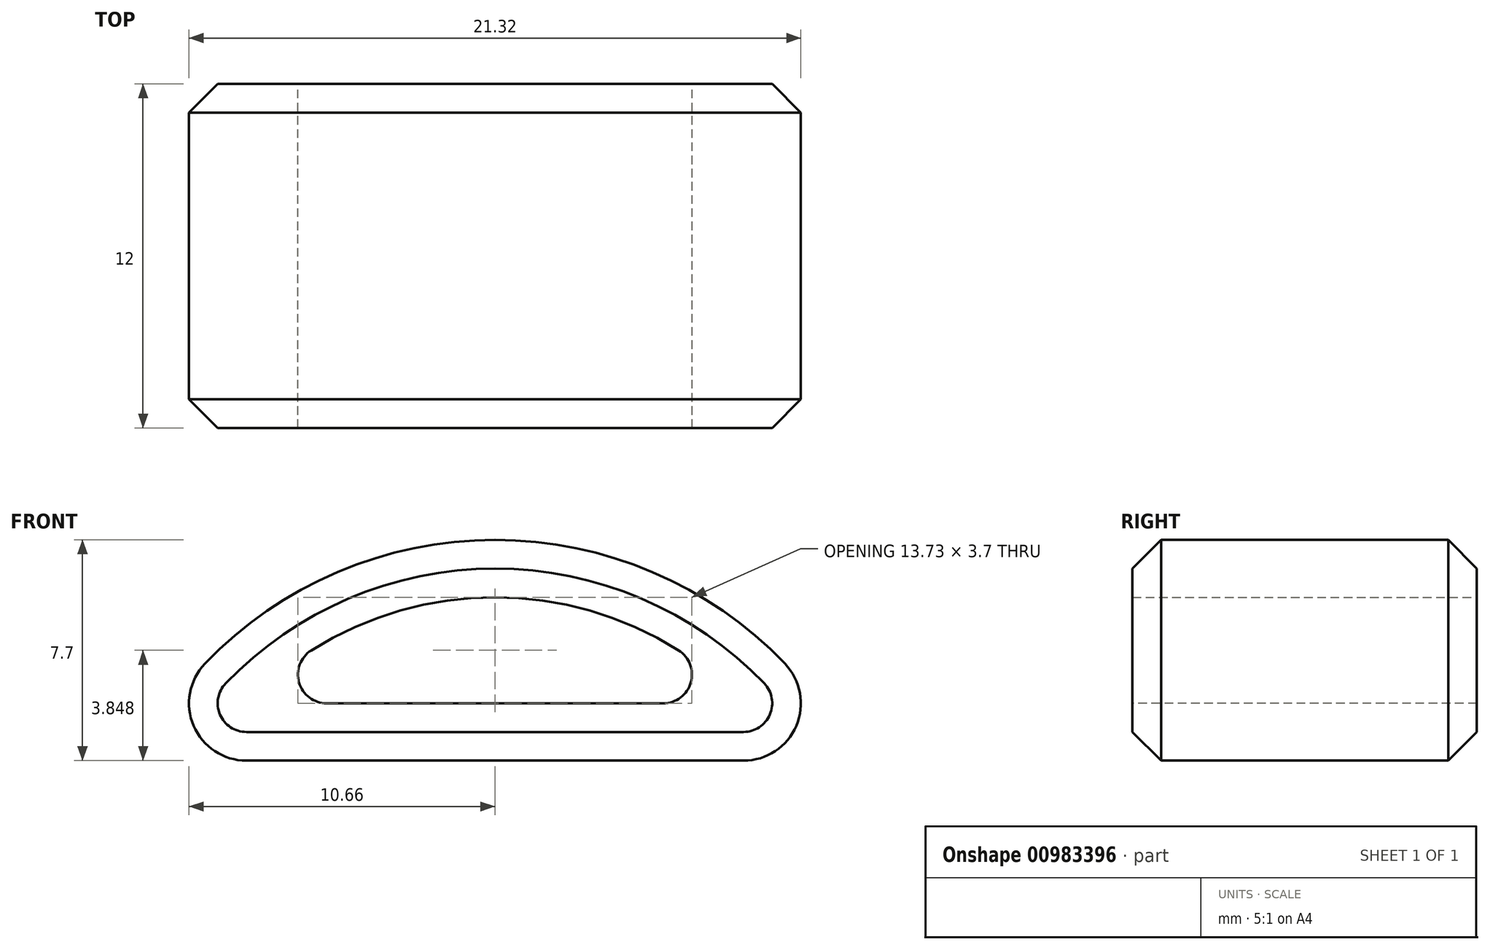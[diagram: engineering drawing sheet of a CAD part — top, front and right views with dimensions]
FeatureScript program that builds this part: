
annotation { "Feature Type Name" : "Feature", "Feature Type Description" : "" }
export const myFeature = defineFeature(function(context is Context, id is Id, definition is map)
    precondition{}
    {
        {
            var Q0;
            Q0=qCreatedBy(makeId("Front.planeOp"),FACE);
            var sketch = newSketch(context, id + "F0", { "sketchPlane" : qUnion([Q0])});
            skArc(sketch, "E0", {"start": v(12.5, 0) * mm, "mid": v(0, 7.7) * mm, "end": v(-12.5, 0) * mm});
            skLineSegment(sketch, "E1", {"start": v(-12.5, 0) * mm, "end": v(12.5, 0) * mm});
            skSolve(sketch);
        }
        {
            var Q0;
            Q0=makeQuery(id+"F0.imprint","IMPRINT",FACE,{"disambiguationData":[TD([[makeQuery(id+"F0.imprint","IMPRINT",EDGE,{"derivedFrom":sQuery(id+"F0.wireOp",EDGE,"E0")}),1.0]])]});
            extrude(context, id + "F1", {"entities" : qUnion([Q0]), "depth" : 12 * mm, "offsetDistance" : 25 * mm});
        }
        {
            var Q0;
            Q0=makeQuery(id+"F1.opExtrude","CAP_FACE",FACE,{"disambiguationData":[OSD([sQuery(id+"F0.wireOp",EDGE,"E0"),sQuery(id+"F0.wireOp",EDGE,"E1")])],"isStart":false});
            var Q1;
            Q1=makeQuery(id+"F1.opExtrude","CAP_FACE",FACE,{"disambiguationData":[OSD([sQuery(id+"F0.wireOp",EDGE,"E0"),sQuery(id+"F0.wireOp",EDGE,"E1")])],"isStart":true});
            shell(context, id + "F2", {"entities" : qUnion([Q0, Q1]), "thickness" : 2 * mm});
        }
        {
            var Q0;
            {var subQ0=sQuery(id+"F0.wireOp",EDGE,"E1");var subQ1=sQuery(id+"F0.wireOp",EDGE,"E0");Q0=makeQuery(id+"F1.opExtrude","SWEPT_EDGE",EDGE,{"disambiguationData":[OSD([subQ1,subQ0]),TDD([makeQuery(id+"F0.imprint","INTERSECT",VERTEX,{"disambiguationData":[OD(1.0)],"derivedFrom":[subQ1,subQ0]})])]});}
            var Q1;
            {var subQ0=sQuery(id+"F0.wireOp",EDGE,"E1");var subQ1=sQuery(id+"F0.wireOp",EDGE,"E0");Q1=makeQuery(id+"F1.opExtrude","SWEPT_EDGE",EDGE,{"disambiguationData":[OSD([subQ1,subQ0]),TDD([makeQuery(id+"F0.imprint","INTERSECT",VERTEX,{"disambiguationData":[OD(0.0)],"derivedFrom":[subQ1,subQ0]})])]});}
            fillet(context, id + "F3", {"entities" : qUnion([Q0, Q1]), "radius" : 2 * mm, "tangentPropagation" : true, "allowEdgeOverflow" : false});
        }
        {
            var Q0;
            {var subQ0=sQuery(id+"F0.wireOp",EDGE,"E1");var subQ1=sQuery(id+"F0.wireOp",EDGE,"E0");Q0=makeQuery(id+"F2.opShell","OFFSET_EDGE",EDGE,{"disambiguationData":[OSD([subQ1,subQ0]),TDD([makeQuery(id+"F1.opExtrude","SWEPT_EDGE",EDGE,{"disambiguationData":[OSD([subQ1,subQ0]),TDD([makeQuery(id+"F0.imprint","INTERSECT",VERTEX,{"disambiguationData":[OD(1.0)],"derivedFrom":[subQ1,subQ0]})])]})])]});}
            var Q1;
            {var subQ0=sQuery(id+"F0.wireOp",EDGE,"E1");var subQ1=sQuery(id+"F0.wireOp",EDGE,"E0");Q1=makeQuery(id+"F2.opShell","OFFSET_EDGE",EDGE,{"disambiguationData":[OSD([subQ1,subQ0]),TDD([makeQuery(id+"F1.opExtrude","SWEPT_EDGE",EDGE,{"disambiguationData":[OSD([subQ1,subQ0]),TDD([makeQuery(id+"F0.imprint","INTERSECT",VERTEX,{"disambiguationData":[OD(0.0)],"derivedFrom":[subQ1,subQ0]})])]})])]});}
            fillet(context, id + "F4", {"entities" : qUnion([Q0, Q1]), "radius" : 1 * mm, "tangentPropagation" : true, "allowEdgeOverflow" : false});
        }
        {
            var Q0;
            Q0=makeQuery(id+"F1.opExtrude","CAP_EDGE",EDGE,{"disambiguationData":[OSD([sQuery(id+"F0.wireOp",EDGE,"E0")])],"isStart":false});
            var Q1;
            Q1=makeQuery(id+"F1.opExtrude","CAP_EDGE",EDGE,{"disambiguationData":[OSD([sQuery(id+"F0.wireOp",EDGE,"E0")])],"isStart":true});
            chamfer(context, id + "F5", {"entities" : qUnion([Q0, Q1]), "width" : 1 * mm, "tangentPropagation" : true});
        }
    });
